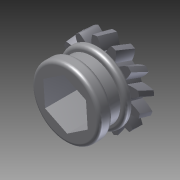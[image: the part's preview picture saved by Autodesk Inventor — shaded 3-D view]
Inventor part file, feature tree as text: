
AUTODESK INVENTOR PART (.ipt)
format: ipt  version: 2012 (Build 160160000, 160)  size: 860,672 bytes
history: native  units: in
note: dims shown in document units (in); Inventor stores cm internally (conversion verified against a paired STEP export)
features: sketch x8, extrude x8, fillet x7, other x3, plane x3
ambient origin geometry x8: Origin, YZ Plane, XZ Plane, XY Plane, X Axis, Y Axis, Z Axis, Center Point
bodies: Solid1 (feature_tree)
feature tree (29):
  other  "LargeGearInput.iam"
  other  "Spur Gear2:1"
  other  "BlankLargeGearMotorInput.ipt:1"
  plane  "Work Plane1"
  sketch  "Sketch4"  dims[d0=0.3937in d5=0.3937in d6=0.0in]
  plane  "Work Plane2"
  extrude  "Extrusion3"  Depth=0.3937in TaperAngle=0.0deg
  extrude  "Extrusion4"  Depth=0.6496in
  extrude  "Extrusion5"  Depth=0.3937in TaperAngle=0.0deg
  extrude  "Extrusion6"  Depth=0.2402in
  extrude  "Extrusion7"  Depth=0.3937in TaperAngle=0.0deg
  extrude  "Extrusion8"  Depth=0.1378in TaperAngle=0.0deg
  plane  "Work Plane3"
  extrude  "Extrusion9"  Depth=0.0787in TaperAngle=0.0deg
  fillet  "Fillet2"  Radius=0.0197in
  fillet  "Fillet3"  Radius=0.0151in
  fillet  "Fillet4"  Radius=0.0394in
  fillet  "Fillet5"  Radius=0.0197in
  extrude  "Extrusion10"  Depth=0.0394in
  fillet  "Fillet6"  Radius=0.0394in
  fillet  "Fillet7"  Radius=0.0394in
  fillet  "Fillet8"  [1 undecoded]
  sketch  "Sketch5"  dims[d7=0.0118in d8=0.0in d9=0.6496in]
  sketch  "Sketch6"  dims[d10=0.4803in d11=0.3937in d12=0.0in]
  sketch  "Sketch7"  dims[d13=0.3937in d14=0.0in d15=0.2402in]
  sketch  "Sketch8"  dims[d16=0.4803in d17=0.3937in d18=0.0in]
  sketch  "Sketch10"  dims[d19=0.0591in d20=0.1378in d21=0.0in]
  sketch  "Sketch11"  dims[d22=0.1535in d23=0.0787in d24=0.0in d26=0.0197in d27=0.0151in d28=0.0394in d29=0.0197in]
  sketch  "Sketch12"  dims[d30=0.0118in d31=0.0in d32=0.0394in d33=0.0394in d34=0.0394in]
note: 1 required parameter value undecoded (feature->parameter linkage not recoverable at this tier; creation-order binding heuristic only, values carry confidence <= 0.55)
